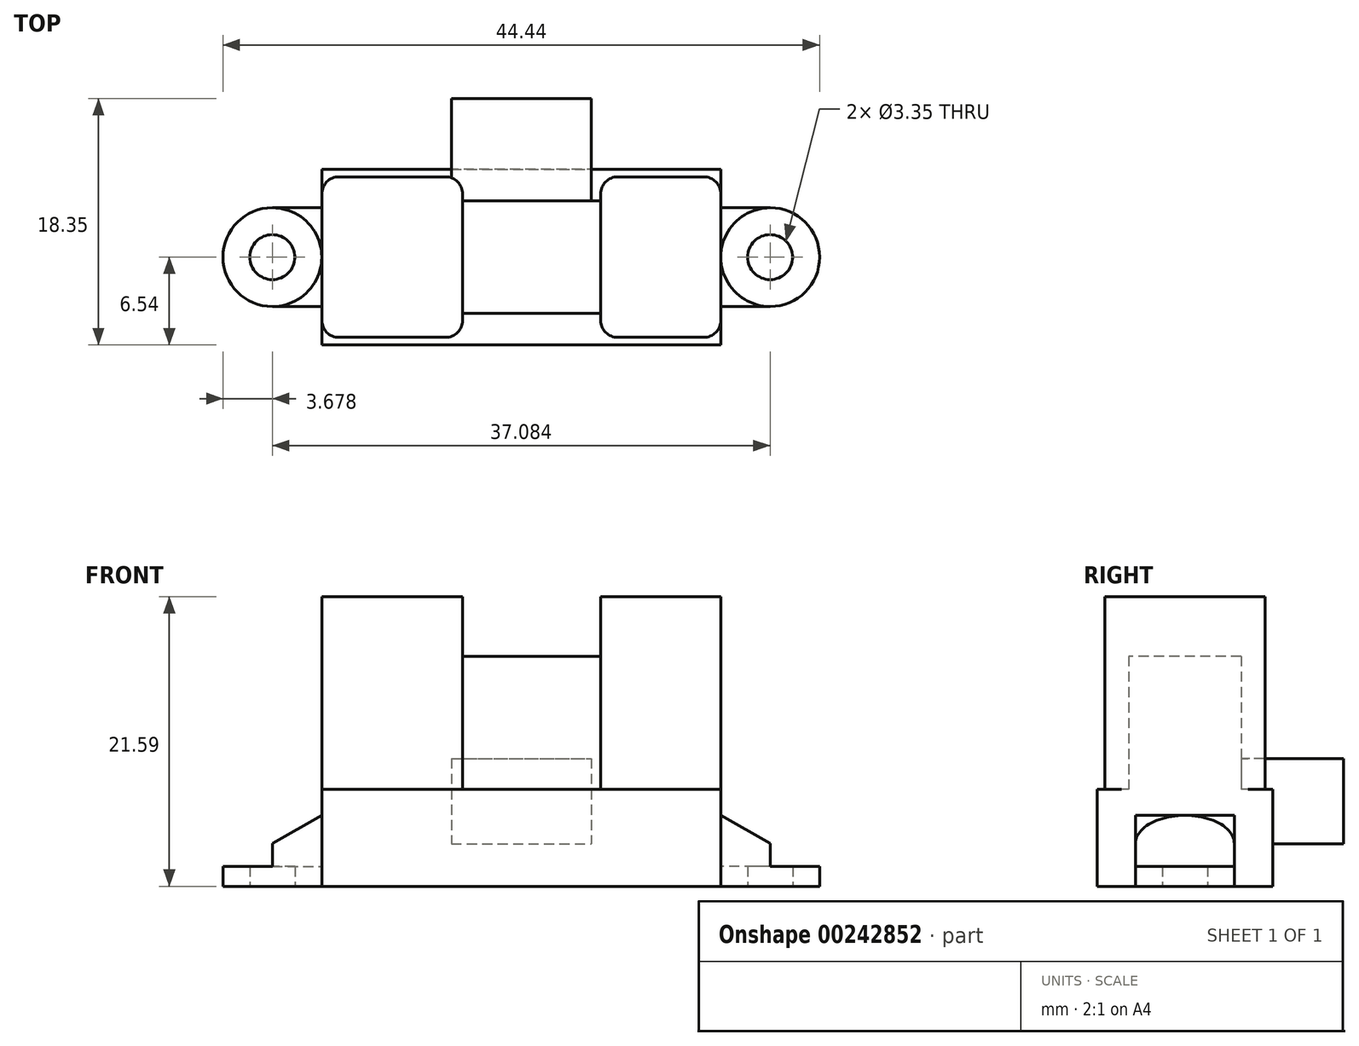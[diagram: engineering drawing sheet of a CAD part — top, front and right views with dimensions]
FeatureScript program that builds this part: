
annotation { "Feature Type Name" : "Feature", "Feature Type Description" : "" }
export const myFeature = defineFeature(function(context is Context, id is Id, definition is map)
    precondition{}
    {
        {
            var Q0;
            Q0=qCreatedBy(makeId("Top.planeOp"),FACE);
            var sketch = newSketch(context, id + "F0", { "sketchPlane" : qUnion([Q0])});
            skLineSegment(sketch, "E0.bottom", {"start": v(14.86, 6.54) * mm, "end": v(-14.86, 6.54) * mm});
            skLineSegment(sketch, "E0.top", {"start": v(14.86, -6.54) * mm, "end": v(-14.86, -6.54) * mm});
            skLineSegment(sketch, "E0.left", {"start": v(14.86, 6.54) * mm, "end": v(14.86, -6.54) * mm});
            skLineSegment(sketch, "E0.right", {"start": v(-14.86, 6.54) * mm, "end": v(-14.86, -6.54) * mm});
            skPoint(sketch, "E0.middle", {"position": v(0, 0) * mm});
            skCircle(sketch, "E1", {"center": v(18.54, 0) * mm, "radius": 3.68 * mm});
            skCircle(sketch, "E2", {"center": v(18.54, 0) * mm, "radius": 1.68 * mm});
            skLineSegment(sketch, "E3", {"start": v(18.54, 3.68) * mm, "end": v(14.86, 3.68) * mm});
            skLineSegment(sketch, "E4", {"start": v(14.86, -3.68) * mm, "end": v(18.54, -3.68) * mm});
            skCircle(sketch, "E5.MirrorC", {"center": v(-18.54, 0) * mm, "radius": 3.68 * mm});
            skLineSegment(sketch, "E6.MirrorCS", {"start": v(-18.54, 3.68) * mm, "end": v(-14.86, 3.68) * mm});
            skCircle(sketch, "E7.MirrorC", {"center": v(-18.54, 0) * mm, "radius": 1.68 * mm});
            skLineSegment(sketch, "E8.MirrorCS", {"start": v(-14.86, -3.68) * mm, "end": v(-18.54, -3.68) * mm});
            skSolve(sketch);
        }
        {
            var Q0;
            Q0 = qSketchRegion(id + "F0", true);
            extrude(context, id + "F1", {"entities" : qUnion([Q0]), "depth" : 1.47 * mm});
        }
        {
            var Q0;
            Q0=makeQuery(id+"F1.opExtrude","CAP_FACE",FACE,{"disambiguationData":[OSD([sQuery(id+"F0.wireOp",EDGE,"E0.bottom"),sQuery(id+"F0.wireOp",EDGE,"E0.top"),sQuery(id+"F0.wireOp",EDGE,"E0.left"),sQuery(id+"F0.wireOp",EDGE,"E0.right"),sQuery(id+"F0.wireOp",EDGE,"E1"),sQuery(id+"F0.wireOp",EDGE,"E2"),sQuery(id+"F0.wireOp",EDGE,"E3"),sQuery(id+"F0.wireOp",EDGE,"E4"),sQuery(id+"F0.wireOp",EDGE,"E5.MirrorC"),sQuery(id+"F0.wireOp",EDGE,"E6.MirrorCS"),sQuery(id+"F0.wireOp",EDGE,"E7.MirrorC"),sQuery(id+"F0.wireOp",EDGE,"E8.MirrorCS")])],"isStart":false});
            var sketch = newSketch(context, id + "F2", { "sketchPlane" : qUnion([Q0])});
            skArc(sketch, "E9.0", {"start": v(-18.54, 3.68) * mm, "mid": v(-14.86, 0) * mm, "end": v(-18.54, -3.68) * mm});
            skLineSegment(sketch, "E10.0", {"start": v(-14.86, 3.68) * mm, "end": v(-14.86, -3.68) * mm});
            skArc(sketch, "E11", {"start": v(-18.54, -3.68) * mm, "mid": v(-14.86, 0) * mm, "end": v(-18.54, 3.68) * mm});
            skLineSegment(sketch, "E12.0", {"start": v(-18.54, 3.68) * mm, "end": v(-14.86, 3.68) * mm});
            skLineSegment(sketch, "E13.0", {"start": v(-14.86, -3.68) * mm, "end": v(-18.54, -3.68) * mm});
            skPoint(sketch, "E14.orphan", {"position": v(-14.86, 6.54) * mm});
            skPoint(sketch, "E15.orphan", {"position": v(-14.86, -6.54) * mm});
            skPoint(sketch, "E16.orphan", {"position": v(14.86, -6.54) * mm});
            skPoint(sketch, "E17.orphan", {"position": v(14.86, 6.54) * mm});
            skArc(sketch, "E18.MirrorCS", {"start": v(18.54, -3.68) * mm, "mid": v(14.86, 0) * mm, "end": v(18.54, 3.68) * mm});
            skLineSegment(sketch, "E19.MirrorCS", {"start": v(18.54, 3.68) * mm, "end": v(14.86, 3.68) * mm});
            skLineSegment(sketch, "E20.MirrorCS", {"start": v(14.86, 3.68) * mm, "end": v(14.86, -3.68) * mm});
            skLineSegment(sketch, "E21.MirrorCS", {"start": v(14.86, -3.68) * mm, "end": v(18.54, -3.68) * mm});
            skSolve(sketch);
        }
        {
            var Q0;
            Q0 = qSketchRegion(id + "F2", true);
            extrude(context, id + "F3", {"entities" : qUnion([Q0]), "depth" : 3.8 * mm});
        }
        {
            var Q0;
            Q0=makeQuery(id+"F3.opExtrude","SWEPT_FACE",FACE,{"disambiguationData":[OSD([sQuery(id+"F2.wireOp",EDGE,"E13.0")])]});
            var sketch = newSketch(context, id + "F4", { "sketchPlane" : qUnion([Q0])});
            skLineSegment(sketch, "E22", {"start": v(-18.54, 3.2) * mm, "end": v(-18.54, 5.28) * mm});
            skLineSegment(sketch, "E23", {"start": v(-18.54, 3.2) * mm, "end": v(-14.86, 5.28) * mm});
            skLineSegment(sketch, "E24.0", {"start": v(-14.86, 5.28) * mm, "end": v(-18.54, 5.28) * mm});
            skLineSegment(sketch, "E25.MirrorCS", {"start": v(18.54, 3.2) * mm, "end": v(14.86, 5.28) * mm});
            skLineSegment(sketch, "E26.MirrorCS", {"start": v(14.86, 5.28) * mm, "end": v(18.54, 5.28) * mm});
            skLineSegment(sketch, "E27.MirrorCS", {"start": v(18.54, 3.2) * mm, "end": v(18.54, 5.28) * mm});
            skSolve(sketch);
        }
        {
            var Q0;
            Q0 = qSketchRegion(id + "F4", true);
            var Q1;
            Q1=makeQuery(id+"F3.opExtrude","SWEPT_FACE",FACE,{"disambiguationData":[OSD([sQuery(id+"F2.wireOp",EDGE,"E12.0")])]});
            extrude(context, id + "F5", {"entities" : qUnion([Q0]), "operationType" : NewBodyOperationType.REMOVE, "endBound" : BoundingType.UP_TO_SURFACE, "oppositeDirection" : true, "endBoundEntityFace" : qUnion([Q1]), "depth" : 25.4 * mm});
        }
        {
            var Q0;
            Q0=qCreatedBy(makeId("Top.planeOp"),FACE);
            var sketch = newSketch(context, id + "F6", { "sketchPlane" : qUnion([Q0])});
            skLineSegment(sketch, "E28.0", {"start": v(14.86, 6.54) * mm, "end": v(-14.86, 6.54) * mm});
            skLineSegment(sketch, "E29.0", {"start": v(-14.86, 6.54) * mm, "end": v(-14.86, 3.68) * mm});
            skLineSegment(sketch, "E30.0", {"start": v(-14.86, 3.68) * mm, "end": v(-14.86, 0) * mm});
            skLineSegment(sketch, "E31.0", {"start": v(-14.86, 0) * mm, "end": v(-14.86, -3.68) * mm});
            skLineSegment(sketch, "E32.0", {"start": v(-14.86, -3.68) * mm, "end": v(-14.86, -6.54) * mm});
            skLineSegment(sketch, "E33.0", {"start": v(14.86, -6.54) * mm, "end": v(-14.86, -6.54) * mm});
            skPoint(sketch, "E34.0", {"position": v(14.86, -5.11) * mm});
            skLineSegment(sketch, "E35.0", {"start": v(14.86, 0) * mm, "end": v(14.86, -3.68) * mm});
            skLineSegment(sketch, "E36.0", {"start": v(14.86, 3.68) * mm, "end": v(14.86, 0) * mm});
            skPoint(sketch, "E37.0", {"position": v(14.86, 5.11) * mm});
            skLineSegment(sketch, "E38.0", {"start": v(14.86, 6.54) * mm, "end": v(14.86, 3.68) * mm});
            skLineSegment(sketch, "E39.0", {"start": v(14.86, -3.68) * mm, "end": v(14.86, -6.54) * mm});
            skSolve(sketch);
        }
        {
            var Q0;
            Q0 = qSketchRegion(id + "F6", true);
            extrude(context, id + "F7", {"entities" : qUnion([Q0]), "operationType" : NewBodyOperationType.ADD, "depth" : 7.24 * mm});
        }
        {
            var Q0;
            Q0=makeQuery(id+"F7.opExtrude","CAP_FACE",FACE,{"disambiguationData":[OSD([sQuery(id+"F6.wireOp",EDGE,"E28.0"),sQuery(id+"F6.wireOp",EDGE,"E29.0"),sQuery(id+"F6.wireOp",EDGE,"E30.0"),sQuery(id+"F6.wireOp",EDGE,"E31.0"),sQuery(id+"F6.wireOp",EDGE,"E32.0"),sQuery(id+"F6.wireOp",EDGE,"E33.0"),sQuery(id+"F6.wireOp",EDGE,"E35.0"),sQuery(id+"F6.wireOp",EDGE,"E36.0"),sQuery(id+"F6.wireOp",EDGE,"E38.0"),sQuery(id+"F6.wireOp",EDGE,"E39.0")])],"isStart":false});
            var sketch = newSketch(context, id + "F8", { "sketchPlane" : qUnion([Q0])});
            skLineSegment(sketch, "E40.bottom", {"start": v(-5.64, 5.98) * mm, "end": v(-13.59, 5.98) * mm});
            skLineSegment(sketch, "E40.top", {"start": v(-5.64, -5.98) * mm, "end": v(-13.59, -5.98) * mm});
            skLineSegment(sketch, "E40.left", {"start": v(-4.37, 4.71) * mm, "end": v(-4.37, -4.71) * mm});
            skLineSegment(sketch, "E40.right", {"start": v(-14.86, 4.71) * mm, "end": v(-14.86, -4.71) * mm});
            skPoint(sketch, "E40.middle", {"position": v(-9.61, 0) * mm});
            skPoint(sketch, "E41.visualSharp", {"position": v(-14.86, 5.98) * mm});
            skArc(sketch, "E41.filletArc", {"start": v(-13.59, 5.98) * mm, "mid": v(-14.49, 5.6) * mm, "end": v(-14.86, 4.71) * mm});
            skPoint(sketch, "E42.visualSharp", {"position": v(-4.37, 5.98) * mm});
            skArc(sketch, "E42.filletArc", {"start": v(-4.37, 4.71) * mm, "mid": v(-4.74, 5.6) * mm, "end": v(-5.64, 5.98) * mm});
            skPoint(sketch, "E43.visualSharp", {"position": v(-4.37, -5.98) * mm});
            skArc(sketch, "E43.filletArc", {"start": v(-5.64, -5.98) * mm, "mid": v(-4.74, -5.6) * mm, "end": v(-4.37, -4.71) * mm});
            skPoint(sketch, "E44.visualSharp", {"position": v(-14.86, -5.98) * mm});
            skArc(sketch, "E44.filletArc", {"start": v(-14.86, -4.71) * mm, "mid": v(-14.49, -5.6) * mm, "end": v(-13.59, -5.98) * mm});
            skLineSegment(sketch, "E45.bottom", {"start": v(13.59, 5.98) * mm, "end": v(7.19, 5.98) * mm});
            skLineSegment(sketch, "E45.top", {"start": v(13.59, -5.98) * mm, "end": v(7.19, -5.98) * mm});
            skLineSegment(sketch, "E45.left", {"start": v(14.86, 4.71) * mm, "end": v(14.86, -4.71) * mm});
            skLineSegment(sketch, "E45.right", {"start": v(5.92, 4.71) * mm, "end": v(5.92, -4.71) * mm});
            skPoint(sketch, "E45.middle", {"position": v(10.39, 0) * mm});
            skPoint(sketch, "E46.visualSharp", {"position": v(5.92, 5.98) * mm});
            skArc(sketch, "E46.filletArc", {"start": v(7.19, 5.98) * mm, "mid": v(6.3, 5.6) * mm, "end": v(5.92, 4.71) * mm});
            skPoint(sketch, "E47.visualSharp", {"position": v(14.86, 5.98) * mm});
            skArc(sketch, "E47.filletArc", {"start": v(14.86, 4.71) * mm, "mid": v(14.49, 5.6) * mm, "end": v(13.59, 5.98) * mm});
            skPoint(sketch, "E48.visualSharp", {"position": v(14.86, -5.98) * mm});
            skArc(sketch, "E48.filletArc", {"start": v(13.59, -5.98) * mm, "mid": v(14.49, -5.6) * mm, "end": v(14.86, -4.71) * mm});
            skPoint(sketch, "E49.visualSharp", {"position": v(5.92, -5.98) * mm});
            skArc(sketch, "E49.filletArc", {"start": v(5.92, -4.71) * mm, "mid": v(6.3, -5.6) * mm, "end": v(7.19, -5.98) * mm});
            skSolve(sketch);
        }
        {
            var Q0;
            Q0 = qSketchRegion(id + "F8", true);
            extrude(context, id + "F9", {"entities" : qUnion([Q0]), "operationType" : NewBodyOperationType.ADD, "depth" : 14.35 * mm});
        }
        {
            var Q0;
            Q0=makeQuery(id+"F7.opExtrude","CAP_FACE",FACE,{"disambiguationData":[OSD([sQuery(id+"F6.wireOp",EDGE,"E28.0"),sQuery(id+"F6.wireOp",EDGE,"E29.0"),sQuery(id+"F6.wireOp",EDGE,"E30.0"),sQuery(id+"F6.wireOp",EDGE,"E31.0"),sQuery(id+"F6.wireOp",EDGE,"E32.0"),sQuery(id+"F6.wireOp",EDGE,"E33.0"),sQuery(id+"F6.wireOp",EDGE,"E35.0"),sQuery(id+"F6.wireOp",EDGE,"E36.0"),sQuery(id+"F6.wireOp",EDGE,"E38.0"),sQuery(id+"F6.wireOp",EDGE,"E39.0")])],"isStart":false});
            var sketch = newSketch(context, id + "F10", { "sketchPlane" : qUnion([Q0])});
            skLineSegment(sketch, "E50.bottom", {"start": v(5.92, 4.2) * mm, "end": v(-4.37, 4.2) * mm});
            skLineSegment(sketch, "E50.top", {"start": v(5.92, -4.2) * mm, "end": v(-4.37, -4.2) * mm});
            skLineSegment(sketch, "E50.left", {"start": v(5.92, 4.2) * mm, "end": v(5.92, -4.2) * mm});
            skLineSegment(sketch, "E50.right", {"start": v(-4.37, 4.2) * mm, "end": v(-4.37, -4.2) * mm});
            skPoint(sketch, "E50.middle", {"position": v(0.77, 0) * mm});
            skSolve(sketch);
        }
        {
            var Q0;
            Q0 = qSketchRegion(id + "F10", true);
            extrude(context, id + "F11", {"entities" : qUnion([Q0]), "operationType" : NewBodyOperationType.ADD, "depth" : 9.9 * mm});
        }
        {
            var Q0;
            Q0=makeQuery(id+"F11.opExtrude","SWEPT_FACE",FACE,{"disambiguationData":[OSD([sQuery(id+"F10.wireOp",EDGE,"E50.bottom")])]});
            var sketch = newSketch(context, id + "F12", { "sketchPlane" : qUnion([Q0])});
            skLineSegment(sketch, "E51.bottom", {"start": v(5.2, 9.53) * mm, "end": v(-5.2, 9.53) * mm});
            skLineSegment(sketch, "E51.top", {"start": v(5.2, 3.18) * mm, "end": v(-5.2, 3.18) * mm});
            skLineSegment(sketch, "E51.left", {"start": v(5.2, 9.53) * mm, "end": v(5.2, 3.18) * mm});
            skLineSegment(sketch, "E51.right", {"start": v(-5.2, 9.53) * mm, "end": v(-5.2, 3.18) * mm});
            skPoint(sketch, "E51.middle", {"position": v(0, 6.35) * mm});
            skSolve(sketch);
        }
        {
            var Q0;
            Q0 = qSketchRegion(id + "F12", true);
            extrude(context, id + "F13", {"entities" : qUnion([Q0]), "operationType" : NewBodyOperationType.ADD, "depth" : 7.62 * mm});
        }
    });
